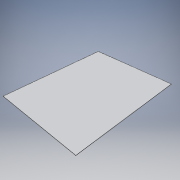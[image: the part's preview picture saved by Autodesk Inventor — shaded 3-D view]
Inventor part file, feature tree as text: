
AUTODESK INVENTOR PART (.ipt)
format: ipt  version: 2019 (Build 230136000, 136)  size: 93,696 bytes
history: native  units: in
note: dims shown in document units (in); Inventor stores cm internally (conversion verified against a paired STEP export)
features: extrude x1, sketch x1
ambient origin geometry x8: Origin, YZ Plane, XZ Plane, XY Plane, X Axis, Y Axis, Z Axis, Center Point
bodies: Solid1 (feature_tree)
feature tree (2):
  extrude  "Extrusion1"  Depth=20.0in
  sketch  "Sketch1"  dims[d0=14.0in d1=20.0in d2=0.0625in d3=0.0in]
